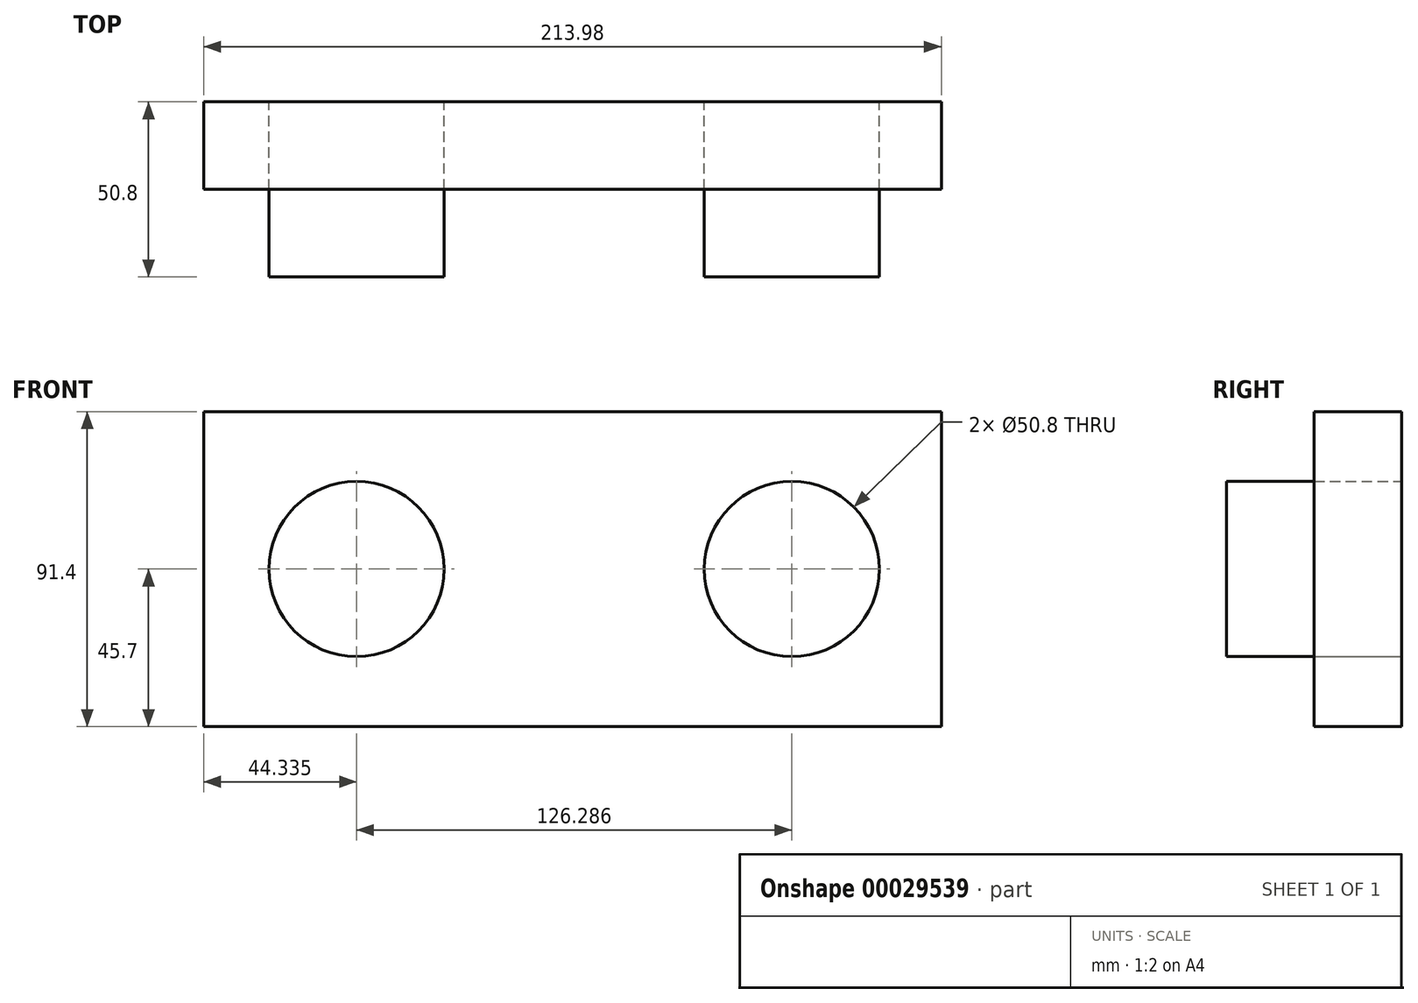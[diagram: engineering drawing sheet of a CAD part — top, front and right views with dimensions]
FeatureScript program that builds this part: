
annotation { "Feature Type Name" : "Feature", "Feature Type Description" : "" }
export const myFeature = defineFeature(function(context is Context, id is Id, definition is map)
    precondition{}
    {
        {
            var Q0;
            Q0=qCreatedBy(makeId("Front.planeOp"),FACE);
            var sketch = newSketch(context, id + "F0", { "sketchPlane" : qUnion([Q0])});
            skCircle(sketch, "E0", {"center": v(-50.18, 0) * mm, "radius": 25.4 * mm});
            skCircle(sketch, "E1", {"center": v(76.11, 0) * mm, "radius": 25.4 * mm});
            skLineSegment(sketch, "E2.rect.bottom", {"start": v(119.47, -45.7) * mm, "end": v(-94.51, -45.7) * mm});
            skLineSegment(sketch, "E2.rect.top", {"start": v(119.47, 45.7) * mm, "end": v(-94.51, 45.7) * mm});
            skLineSegment(sketch, "E2.rect.left", {"start": v(119.47, -45.7) * mm, "end": v(119.47, 45.7) * mm});
            skLineSegment(sketch, "E2.rect.right", {"start": v(-94.51, -45.7) * mm, "end": v(-94.51, 45.7) * mm});
            skPoint(sketch, "E2.rect.middle", {"position": v(12.48, 0) * mm});
            skSolve(sketch);
        }
        {
            var Q0;
            Q0=makeQuery(id+"F0.imprint","IMPRINT",FACE,{"disambiguationData":[TD([[makeQuery(id+"F0.imprint","IMPRINT",EDGE,{"derivedFrom":sQuery(id+"F0.wireOp",EDGE,"E0")}),1.0]])]});
            var Q1;
            Q1=makeQuery(id+"F0.imprint","IMPRINT",FACE,{"disambiguationData":[TD([[makeQuery(id+"F0.imprint","IMPRINT",EDGE,{"derivedFrom":sQuery(id+"F0.wireOp",EDGE,"E1")}),1.0]])]});
            extrude(context, id + "F1", {"entities" : qUnion([Q0, Q1]), "depth" : 50.8 * mm});
        }
        {
            var Q0;
            Q0 = qSketchRegion(id + "F0", true);
            extrude(context, id + "F2", {"entities" : qUnion([Q0]), "depth" : 25.4 * mm});
        }
    });
